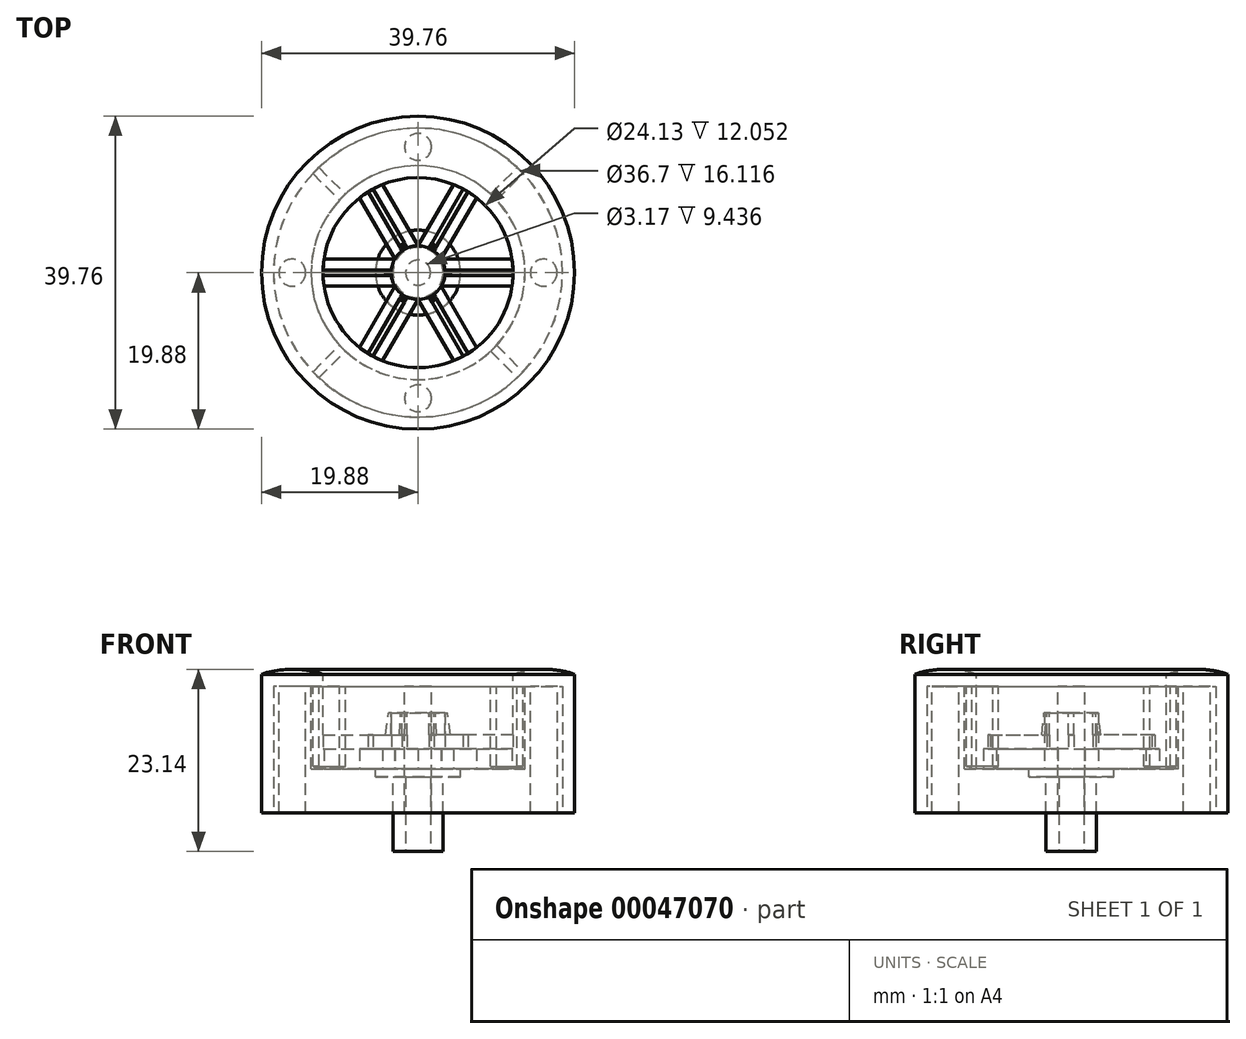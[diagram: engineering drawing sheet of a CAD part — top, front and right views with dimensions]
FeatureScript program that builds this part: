
annotation { "Feature Type Name" : "Feature", "Feature Type Description" : "" }
export const myFeature = defineFeature(function(context is Context, id is Id, definition is map)
    precondition{}
    {
        {
            var Q0;
            Q0=qCreatedBy(makeId("Top.planeOp"),FACE);
            var sketch = newSketch(context, id + "F0", { "sketchPlane" : qUnion([Q0])});
            skCircle(sketch, "E0", {"center": v(0, 0) * mm, "radius": 19.88 * mm});
            skSolve(sketch);
        }
        {
            var Q0;
            Q0=makeQuery(id+"F0.imprint","IMPRINT",FACE,{"disambiguationData":[TD([[makeQuery(id+"F0.imprint","IMPRINT",EDGE,{"derivedFrom":sQuery(id+"F0.wireOp",EDGE,"E0")}),1.0]])]});
            extrude(context, id + "F1", {"entities" : qUnion([Q0]), "endBound" : BoundingType.SYMMETRIC, "depth" : 17.64 * mm});
        }
        {
            var Q0;
            Q0=makeQuery(id+"F1.opExtrude","CAP_FACE",FACE,{"disambiguationData":[OSD([sQuery(id+"F0.wireOp",EDGE,"E0")])],"isStart":true});
            shell(context, id + "F2", {"entities" : qUnion([Q0]), "thickness" : 1.52 * mm});
        }
        {
            var Q0;
            Q0=makeQuery(id+"F1.opExtrude","CAP_FACE",FACE,{"disambiguationData":[OSD([sQuery(id+"F0.wireOp",EDGE,"E0")])],"isStart":false});
            var sketch = newSketch(context, id + "F3", { "sketchPlane" : qUnion([Q0])});
            skCircle(sketch, "E1", {"center": v(0, 0) * mm, "radius": 12.07 * mm});
            skSolve(sketch);
        }
        {
            var Q0;
            Q0 = qSketchRegion(id + "F3", true);
            extrude(context, id + "F4", {"entities" : qUnion([Q0]), "operationType" : NewBodyOperationType.REMOVE, "endBound" : BoundingType.UP_TO_NEXT, "oppositeDirection" : true, "depth" : 25.4 * mm});
        }
        {
            var Q0;
            {var subQ0=sQuery(id+"F0.wireOp",EDGE,"E0");Q0=makeQuery(id+"F2.opShell","OFFSET_FACE",FACE,{"disambiguationData":[OSD([subQ0]),TDD([makeQuery(id+"F1.opExtrude","CAP_FACE",FACE,{"disambiguationData":[OSD([subQ0])],"isStart":false})])]});}
            var sketch = newSketch(context, id + "F5", { "sketchPlane" : qUnion([Q0])});
            skCircle(sketch, "E2", {"center": v(0, 0) * mm, "radius": 13.59 * mm});
            skSolve(sketch);
        }
        {
            var Q0;
            Q0=makeQuery(id+"F5.imprint","IMPRINT",FACE,{"disambiguationData":[TD([[makeQuery(id+"F5.imprint","IMPRINT",EDGE,{"derivedFrom":sQuery(id+"F5.wireOp",EDGE,"E2")}),1.0]])]});
            extrude(context, id + "F6", {"entities" : qUnion([Q0]), "operationType" : NewBodyOperationType.ADD, "depth" : 10.53 * mm});
        }
        {
            var Q0;
            {var subQ0=sQuery(id+"F0.wireOp",EDGE,"E0");Q0=makeQuery(id+"F2.opShell","OFFSET_FACE",FACE,{"disambiguationData":[OSD([subQ0]),TDD([makeQuery(id+"F1.opExtrude","CAP_FACE",FACE,{"disambiguationData":[OSD([subQ0])],"isStart":false})])]});}
            var sketch = newSketch(context, id + "F7", { "sketchPlane" : qUnion([Q0])});
            skCircle(sketch, "E3", {"center": v(0, 15.97) * mm, "radius": 1.7 * mm});
            skLineSegment(sketch, "E4", {"start": v(0, 15.97) * mm, "end": v(0, 18.35) * mm, "construction": true});
            skLineSegment(sketch, "E5", {"start": v(0, 15.97) * mm, "end": v(0, 13.59) * mm, "construction": true});
            skCircle(sketch, "E6.MirrorC", {"center": v(0, -15.97) * mm, "radius": 1.7 * mm});
            skCircle(sketch, "E7", {"center": v(-15.97, 0) * mm, "radius": 1.71 * mm});
            skLineSegment(sketch, "E8", {"start": v(-15.97, 0) * mm, "end": v(-13.59, 0) * mm, "construction": true});
            skLineSegment(sketch, "E9", {"start": v(-15.97, 0) * mm, "end": v(-18.35, 0) * mm, "construction": true});
            skCircle(sketch, "E10.MirrorC", {"center": v(15.97, 0) * mm, "radius": 1.71 * mm});
            skSolve(sketch);
        }
        {
            var Q0;
            Q0 = qSketchRegion(id + "F7", true);
            var Q1;
            Q1=makeQuery(id+"F1.opExtrude","CAP_FACE",FACE,{"disambiguationData":[OSD([sQuery(id+"F0.wireOp",EDGE,"E0")])],"isStart":true});
            extrude(context, id + "F8", {"entities" : qUnion([Q0]), "operationType" : NewBodyOperationType.ADD, "endBound" : BoundingType.UP_TO_SURFACE, "endBoundEntityFace" : qUnion([Q1]), "depth" : 25.4 * mm});
        }
        {
            var Q0;
            Q0=makeQuery(id+"F6.opExtrude","CAP_FACE",FACE,{"disambiguationData":[OSD([sQuery(id+"F0.wireOp",EDGE,"E0"),sQuery(id+"F3.wireOp",EDGE,"E1"),sQuery(id+"F5.wireOp",EDGE,"E2")])],"isStart":false});
            cPlane(context, id + "F9", {"entities" : qUnion([Q0]), "cplaneType" : CPlaneType.OFFSET, "offset" : 0 * mm, "width" : 152.4 * mm, "height" : 152.4 * mm});
        }
        {
            var Q0;
            Q0=qCreatedBy(id+"F9.planeOp",FACE);
            var sketch = newSketch(context, id + "F10", { "sketchPlane" : qUnion([Q0])});
            skCircle(sketch, "E11", {"center": v(0, 0) * mm, "radius": 5.4 * mm});
            skSolve(sketch);
        }
        {
            var Q0;
            Q0=makeQuery(id+"F10.imprint","IMPRINT",FACE,{"disambiguationData":[TD([[makeQuery(id+"F10.imprint","IMPRINT",EDGE,{"derivedFrom":sQuery(id+"F10.wireOp",EDGE,"E11")}),1.0]])]});
            extrude(context, id + "F11", {"entities" : qUnion([Q0]), "depth" : 1.02 * mm});
        }
        {
            var Q0;
            Q0=makeQuery(id+"F11.opExtrude","CAP_FACE",FACE,{"disambiguationData":[OSD([sQuery(id+"F10.wireOp",EDGE,"E11")])],"isStart":true});
            var sketch = newSketch(context, id + "F12", { "sketchPlane" : qUnion([Q0])});
            skCircle(sketch, "E12", {"center": v(0, 0) * mm, "radius": 3.42 * mm});
            skSolve(sketch);
        }
        {
            var Q0;
            Q0=makeQuery(id+"F12.imprint","IMPRINT",FACE,{"disambiguationData":[TD([[makeQuery(id+"F12.imprint","IMPRINT",EDGE,{"derivedFrom":sQuery(id+"F12.wireOp",EDGE,"E12")}),1.0]])]});
            extrude(context, id + "F13", {"entities" : qUnion([Q0]), "operationType" : NewBodyOperationType.ADD, "depth" : 7.11 * mm});
        }
        {
            var Q0;
            Q0=makeQuery(id+"F11.opExtrude","CAP_FACE",FACE,{"disambiguationData":[OSD([sQuery(id+"F10.wireOp",EDGE,"E11")])],"isStart":true});
            var sketch = newSketch(context, id + "F14", { "sketchPlane" : qUnion([Q0])});
            skLineSegment(sketch, "E13", {"start": v(-12.07, 0) * mm, "end": v(-3.42, 0) * mm, "construction": true});
            skLineSegment(sketch, "E14.1.0", {"start": v(6.03, -10.45) * mm, "end": v(1.7, -2.96) * mm, "construction": true});
            skLineSegment(sketch, "E14.2.0", {"start": v(6.03, 10.45) * mm, "end": v(1.7, 2.96) * mm, "construction": true});
            skPoint(sketch, "E14.center", {"position": v(0, 0) * mm});
            skLineSegment(sketch, "E15", {"start": v(4.5, 11.2) * mm, "end": v(0, 3.4) * mm});
            skLineSegment(sketch, "E16", {"start": v(7.44, 9.5) * mm, "end": v(2.94, 1.7) * mm});
            skLineSegment(sketch, "E17.1.0", {"start": v(-11.95, -1.7) * mm, "end": v(-2.94, -1.7) * mm});
            skLineSegment(sketch, "E17.1.1", {"start": v(-11.95, 1.7) * mm, "end": v(-2.94, 1.7) * mm});
            skLineSegment(sketch, "E17.2.0", {"start": v(7.44, -9.5) * mm, "end": v(2.94, -1.7) * mm});
            skLineSegment(sketch, "E17.2.1", {"start": v(4.5, -11.2) * mm, "end": v(0, -3.4) * mm});
            skCircle(sketch, "E18.0", {"center": v(0, 0) * mm, "radius": 3.42 * mm});
            skLineSegment(sketch, "E19.trimOffspring", {"start": v(0, -3.4) * mm, "end": v(-4.5, -11.2) * mm});
            skLineSegment(sketch, "E20.trimOffspring", {"start": v(-1.7, -2.96) * mm, "end": v(-6.03, -10.45) * mm, "construction": true});
            skLineSegment(sketch, "E21.trimOffspring", {"start": v(2.94, -1.7) * mm, "end": v(11.95, -1.7) * mm});
            skLineSegment(sketch, "E22.trimOffspring", {"start": v(-2.94, -1.7) * mm, "end": v(-7.44, -9.5) * mm});
            skLineSegment(sketch, "E23.trimOffspring", {"start": v(-2.94, 1.7) * mm, "end": v(-7.44, 9.5) * mm});
            skLineSegment(sketch, "E24.trimOffspring", {"start": v(2.94, 1.7) * mm, "end": v(11.95, 1.7) * mm});
            skLineSegment(sketch, "E25.trimOffspring", {"start": v(0, 3.4) * mm, "end": v(-4.5, 11.2) * mm});
            skLineSegment(sketch, "E26.trimOffspring", {"start": v(3.42, 0) * mm, "end": v(12.07, 0) * mm, "construction": true});
            skLineSegment(sketch, "E27.trimOffspring", {"start": v(-1.7, 2.96) * mm, "end": v(-6.03, 10.45) * mm, "construction": true});
            skArc(sketch, "E28.0", {"start": v(-11.95, 1.7) * mm, "mid": v(-12.07, 0) * mm, "end": v(-11.95, -1.7) * mm});
            skArc(sketch, "E29.trimOffspring", {"start": v(-4.5, 11.2) * mm, "mid": v(-6.03, 10.45) * mm, "end": v(-7.44, 9.5) * mm});
            skArc(sketch, "E30.trimOffspring", {"start": v(7.44, 9.5) * mm, "mid": v(6.03, 10.45) * mm, "end": v(4.5, 11.2) * mm});
            skArc(sketch, "E31.trimOffspring", {"start": v(11.95, -1.7) * mm, "mid": v(12.07, 0) * mm, "end": v(11.95, 1.7) * mm});
            skArc(sketch, "E32.trimOffspring", {"start": v(4.5, -11.2) * mm, "mid": v(6.03, -10.45) * mm, "end": v(7.44, -9.5) * mm});
            skArc(sketch, "E33.trimOffspring", {"start": v(-7.44, -9.5) * mm, "mid": v(-6.03, -10.45) * mm, "end": v(-4.5, -11.2) * mm});
            skSolve(sketch);
        }
        {
            var Q0;
            {var subQ0=sQuery(id+"F14.wireOp",EDGE,"E28.0");Q0=makeQuery(id+"F14.imprint","IMPRINT",FACE,{"disambiguationData":[TD([[makeQuery(id+"F14.imprint","IMPRINT",EDGE,{"derivedFrom":subQ0}),1.0]])]});}
            var Q1;
            {var subQ0=sQuery(id+"F14.wireOp",EDGE,"E18.0");var subQ1=sQuery(id+"F14.wireOp",EDGE,"E17.1.0");var subQ2=makeQuery(id+"F14.imprint","INTERSECT",VERTEX,{"derivedFrom":[subQ1,subQ0]});Q1=makeQuery(id+"F14.imprint","IMPRINT",FACE,{"disambiguationData":[TD([[makeQuery(id+"F14.imprint","IMPRINT",EDGE,{"disambiguationData":[TD([[subQ2,1.0]])],"derivedFrom":subQ1}),1.0]])]});}
            var Q2;
            {var subQ0=sQuery(id+"F14.wireOp",EDGE,"E25.trimOffspring");var subQ1=sQuery(id+"F14.wireOp",EDGE,"E18.0");var subQ2=makeQuery(id+"F14.imprint","INTERSECT",VERTEX,{"derivedFrom":[subQ1,subQ0]});Q2=makeQuery(id+"F14.imprint","IMPRINT",FACE,{"disambiguationData":[TD([[makeQuery(id+"F14.imprint","IMPRINT",EDGE,{"disambiguationData":[TD([[subQ2,-1.0]])],"derivedFrom":subQ1}),-1.0]])]});}
            var Q3;
            {var subQ0=sQuery(id+"F14.wireOp",EDGE,"E29.trimOffspring");Q3=makeQuery(id+"F14.imprint","IMPRINT",FACE,{"disambiguationData":[TD([[makeQuery(id+"F14.imprint","IMPRINT",EDGE,{"derivedFrom":subQ0}),1.0]])]});}
            var Q4;
            {var subQ0=sQuery(id+"F14.wireOp",EDGE,"E30.trimOffspring");Q4=makeQuery(id+"F14.imprint","IMPRINT",FACE,{"disambiguationData":[TD([[makeQuery(id+"F14.imprint","IMPRINT",EDGE,{"derivedFrom":subQ0}),1.0]])]});}
            var Q5;
            {var subQ0=sQuery(id+"F14.wireOp",EDGE,"E18.0");var subQ1=sQuery(id+"F14.wireOp",EDGE,"E15");var subQ2=makeQuery(id+"F14.imprint","INTERSECT",VERTEX,{"derivedFrom":[subQ1,subQ0]});Q5=makeQuery(id+"F14.imprint","IMPRINT",FACE,{"disambiguationData":[TD([[makeQuery(id+"F14.imprint","IMPRINT",EDGE,{"disambiguationData":[TD([[subQ2,1.0]])],"derivedFrom":subQ1}),1.0]])]});}
            var Q6;
            {var subQ0=sQuery(id+"F14.wireOp",EDGE,"E24.trimOffspring");var subQ1=sQuery(id+"F14.wireOp",EDGE,"E18.0");var subQ2=makeQuery(id+"F14.imprint","INTERSECT",VERTEX,{"derivedFrom":[subQ1,subQ0]});Q6=makeQuery(id+"F14.imprint","IMPRINT",FACE,{"disambiguationData":[TD([[makeQuery(id+"F14.imprint","IMPRINT",EDGE,{"disambiguationData":[TD([[subQ2,1.0]])],"derivedFrom":subQ1}),-1.0]])]});}
            var Q7;
            {var subQ0=sQuery(id+"F14.wireOp",EDGE,"E31.trimOffspring");Q7=makeQuery(id+"F14.imprint","IMPRINT",FACE,{"disambiguationData":[TD([[makeQuery(id+"F14.imprint","IMPRINT",EDGE,{"derivedFrom":subQ0}),1.0]])]});}
            var Q8;
            {var subQ0=sQuery(id+"F14.wireOp",EDGE,"E18.0");var subQ1=sQuery(id+"F14.wireOp",EDGE,"E17.2.0");var subQ2=makeQuery(id+"F14.imprint","INTERSECT",VERTEX,{"derivedFrom":[subQ1,subQ0]});Q8=makeQuery(id+"F14.imprint","IMPRINT",FACE,{"disambiguationData":[TD([[makeQuery(id+"F14.imprint","IMPRINT",EDGE,{"disambiguationData":[TD([[subQ2,1.0]])],"derivedFrom":subQ1}),1.0]])]});}
            var Q9;
            {var subQ0=sQuery(id+"F14.wireOp",EDGE,"E32.trimOffspring");Q9=makeQuery(id+"F14.imprint","IMPRINT",FACE,{"disambiguationData":[TD([[makeQuery(id+"F14.imprint","IMPRINT",EDGE,{"derivedFrom":subQ0}),1.0]])]});}
            var Q10;
            {var subQ0=sQuery(id+"F14.wireOp",EDGE,"E22.trimOffspring");var subQ1=sQuery(id+"F14.wireOp",EDGE,"E18.0");var subQ2=makeQuery(id+"F14.imprint","INTERSECT",VERTEX,{"derivedFrom":[subQ1,subQ0]});Q10=makeQuery(id+"F14.imprint","IMPRINT",FACE,{"disambiguationData":[TD([[makeQuery(id+"F14.imprint","IMPRINT",EDGE,{"disambiguationData":[TD([[subQ2,-1.0]])],"derivedFrom":subQ1}),-1.0]])]});}
            var Q11;
            {var subQ0=sQuery(id+"F14.wireOp",EDGE,"E33.trimOffspring");Q11=makeQuery(id+"F14.imprint","IMPRINT",FACE,{"disambiguationData":[TD([[makeQuery(id+"F14.imprint","IMPRINT",EDGE,{"derivedFrom":subQ0}),1.0]])]});}
            extrude(context, id + "F15", {"entities" : qUnion([Q0, Q1, Q2, Q3, Q4, Q5, Q6, Q7, Q8, Q9, Q10, Q11]), "depth" : 2.54 * mm});
        }
        {
            var Q0;
            Q0=makeQuery(id+"F1.opExtrude","SWEPT_BODY",BODY,{"disambiguationData":[OSD([sQuery(id+"F0.wireOp",EDGE,"E0")])]});
            var Q1;
            Q1=makeQuery(id+"F11.opExtrude","SWEPT_BODY",BODY,{"disambiguationData":[OSD([sQuery(id+"F10.wireOp",EDGE,"E11")])]});
            var Q2;
            Q2=makeQuery(id+"F15.opExtrude","SWEPT_BODY",BODY,{"disambiguationData":[OSD([sQuery(id+"F14.wireOp",EDGE,"E15"),sQuery(id+"F14.wireOp",EDGE,"E16"),sQuery(id+"F14.wireOp",EDGE,"E18.0"),sQuery(id+"F14.wireOp",EDGE,"E30.trimOffspring")])]});
            var Q3;
            Q3=makeQuery(id+"F15.opExtrude","SWEPT_BODY",BODY,{"disambiguationData":[OSD([sQuery(id+"F14.wireOp",EDGE,"E17.1.0"),sQuery(id+"F14.wireOp",EDGE,"E17.1.1"),sQuery(id+"F14.wireOp",EDGE,"E18.0"),sQuery(id+"F14.wireOp",EDGE,"E28.0")])]});
            var Q4;
            Q4=makeQuery(id+"F15.opExtrude","SWEPT_BODY",BODY,{"disambiguationData":[OSD([sQuery(id+"F14.wireOp",EDGE,"E17.2.0"),sQuery(id+"F14.wireOp",EDGE,"E17.2.1"),sQuery(id+"F14.wireOp",EDGE,"E18.0"),sQuery(id+"F14.wireOp",EDGE,"E32.trimOffspring")])]});
            var Q5;
            Q5=makeQuery(id+"F15.opExtrude","SWEPT_BODY",BODY,{"disambiguationData":[OSD([sQuery(id+"F14.wireOp",EDGE,"E18.0"),sQuery(id+"F14.wireOp",EDGE,"E23.trimOffspring"),sQuery(id+"F14.wireOp",EDGE,"E25.trimOffspring"),sQuery(id+"F14.wireOp",EDGE,"E29.trimOffspring")])]});
            var Q6;
            Q6=makeQuery(id+"F15.opExtrude","SWEPT_BODY",BODY,{"disambiguationData":[OSD([sQuery(id+"F14.wireOp",EDGE,"E18.0"),sQuery(id+"F14.wireOp",EDGE,"E19.trimOffspring"),sQuery(id+"F14.wireOp",EDGE,"E22.trimOffspring"),sQuery(id+"F14.wireOp",EDGE,"E33.trimOffspring")])]});
            var Q7;
            Q7=makeQuery(id+"F15.opExtrude","SWEPT_BODY",BODY,{"disambiguationData":[OSD([sQuery(id+"F14.wireOp",EDGE,"E18.0"),sQuery(id+"F14.wireOp",EDGE,"E21.trimOffspring"),sQuery(id+"F14.wireOp",EDGE,"E24.trimOffspring"),sQuery(id+"F14.wireOp",EDGE,"E31.trimOffspring")])]});
            booleanBodies(context, id + "F16", {"operationType" : BooleanOperationType.UNION, "tools" : qUnion([Q0, Q1, Q2, Q3, Q4, Q5, Q6, Q7])});
        }
        {
            var Q0;
            {var subQ0=sQuery(id+"F0.wireOp",EDGE,"E0");Q0=makeQuery(id+"F2.opShell","OFFSET_FACE",FACE,{"disambiguationData":[OSD([subQ0]),TDD([makeQuery(id+"F1.opExtrude","CAP_FACE",FACE,{"disambiguationData":[OSD([subQ0])],"isStart":false})])]});}
            var sketch = newSketch(context, id + "F17", { "sketchPlane" : qUnion([Q0])});
            skArc(sketch, "E34.0", {"start": v(12.6, -13.35) * mm, "mid": v(12.98, -12.98) * mm, "end": v(13.35, -12.6) * mm});
            skArc(sketch, "E35.0", {"start": v(9.22, -9.98) * mm, "mid": v(9.6, -9.6) * mm, "end": v(9.98, -9.22) * mm});
            skLineSegment(sketch, "E36", {"start": v(-14.05, -14.05) * mm, "end": v(14.05, 14.05) * mm, "construction": true});
            skLineSegment(sketch, "E37", {"start": v(-13.35, -12.6) * mm, "end": v(-9.98, -9.22) * mm});
            skLineSegment(sketch, "E38", {"start": v(-12.6, -13.35) * mm, "end": v(-9.22, -9.98) * mm});
            skLineSegment(sketch, "E39", {"start": v(-12.98, 12.98) * mm, "end": v(12.98, -12.98) * mm, "construction": true});
            skLineSegment(sketch, "E40", {"start": v(9.22, -9.98) * mm, "end": v(12.6, -13.35) * mm});
            skLineSegment(sketch, "E41", {"start": v(9.98, -9.22) * mm, "end": v(13.35, -12.6) * mm});
            skArc(sketch, "E42.trimOffspring", {"start": v(-13.35, -12.6) * mm, "mid": v(-12.98, -12.98) * mm, "end": v(-12.6, -13.35) * mm});
            skArc(sketch, "E43.trimOffspring", {"start": v(-9.98, -9.22) * mm, "mid": v(-9.6, -9.6) * mm, "end": v(-9.22, -9.98) * mm});
            skArc(sketch, "E44.MirrorCS", {"start": v(9.22, 9.98) * mm, "mid": v(9.6, 9.6) * mm, "end": v(9.98, 9.22) * mm});
            skArc(sketch, "E45.MirrorCS", {"start": v(-13.35, 12.6) * mm, "mid": v(-12.98, 12.98) * mm, "end": v(-12.6, 13.35) * mm});
            skArc(sketch, "E46.MirrorCS", {"start": v(12.6, 13.35) * mm, "mid": v(12.98, 12.98) * mm, "end": v(13.35, 12.6) * mm});
            skArc(sketch, "E47.MirrorCS", {"start": v(-9.98, 9.22) * mm, "mid": v(-9.6, 9.6) * mm, "end": v(-9.22, 9.98) * mm});
            skLineSegment(sketch, "E48.MirrorCS", {"start": v(-14.05, 14.05) * mm, "end": v(14.05, -14.05) * mm, "construction": true});
            skLineSegment(sketch, "E49.MirrorCS", {"start": v(-13.35, 12.6) * mm, "end": v(-9.98, 9.22) * mm});
            skLineSegment(sketch, "E50.MirrorCS", {"start": v(-12.6, 13.35) * mm, "end": v(-9.22, 9.98) * mm});
            skLineSegment(sketch, "E51.MirrorCS", {"start": v(-12.98, -12.98) * mm, "end": v(12.98, 12.98) * mm, "construction": true});
            skLineSegment(sketch, "E52.MirrorCS", {"start": v(9.98, 9.22) * mm, "end": v(13.35, 12.6) * mm});
            skLineSegment(sketch, "E53.MirrorCS", {"start": v(9.22, 9.98) * mm, "end": v(12.6, 13.35) * mm});
            skSolve(sketch);
        }
        {
            var Q0;
            Q0 = qSketchRegion(id + "F17", true);
            var Q1;
            {var subQ0=sQuery(id+"F14.wireOp",EDGE,"E18.0");Q1=makeQuery(id+"F16.opBoolean","MERGE",FACE,{"derivedFrom":[makeQuery(id+"F6.opExtrude","CAP_FACE",FACE,{"disambiguationData":[OSD([sQuery(id+"F0.wireOp",EDGE,"E0"),sQuery(id+"F3.wireOp",EDGE,"E1"),sQuery(id+"F5.wireOp",EDGE,"E2")])],"isStart":false}),makeQuery(id+"F15.opExtrude","CAP_FACE",FACE,{"disambiguationData":[OSD([sQuery(id+"F14.wireOp",EDGE,"E15"),sQuery(id+"F14.wireOp",EDGE,"E16"),subQ0,sQuery(id+"F14.wireOp",EDGE,"E30.trimOffspring")])],"isStart":true}),makeQuery(id+"F15.opExtrude","CAP_FACE",FACE,{"disambiguationData":[OSD([sQuery(id+"F14.wireOp",EDGE,"E17.1.0"),sQuery(id+"F14.wireOp",EDGE,"E17.1.1"),subQ0,sQuery(id+"F14.wireOp",EDGE,"E28.0")])],"isStart":true}),makeQuery(id+"F15.opExtrude","CAP_FACE",FACE,{"disambiguationData":[OSD([sQuery(id+"F14.wireOp",EDGE,"E17.2.0"),sQuery(id+"F14.wireOp",EDGE,"E17.2.1"),subQ0,sQuery(id+"F14.wireOp",EDGE,"E32.trimOffspring")])],"isStart":true}),makeQuery(id+"F15.opExtrude","CAP_FACE",FACE,{"disambiguationData":[OSD([subQ0,sQuery(id+"F14.wireOp",EDGE,"E23.trimOffspring"),sQuery(id+"F14.wireOp",EDGE,"E25.trimOffspring"),sQuery(id+"F14.wireOp",EDGE,"E29.trimOffspring")])],"isStart":true}),makeQuery(id+"F15.opExtrude","CAP_FACE",FACE,{"disambiguationData":[OSD([subQ0,sQuery(id+"F14.wireOp",EDGE,"E19.trimOffspring"),sQuery(id+"F14.wireOp",EDGE,"E22.trimOffspring"),sQuery(id+"F14.wireOp",EDGE,"E33.trimOffspring")])],"isStart":true}),makeQuery(id+"F15.opExtrude","CAP_FACE",FACE,{"disambiguationData":[OSD([subQ0,sQuery(id+"F14.wireOp",EDGE,"E21.trimOffspring"),sQuery(id+"F14.wireOp",EDGE,"E24.trimOffspring"),sQuery(id+"F14.wireOp",EDGE,"E31.trimOffspring")])],"isStart":true})]});}
            extrude(context, id + "F18", {"entities" : qUnion([Q0]), "operationType" : NewBodyOperationType.ADD, "endBoundEntityFace" : qUnion([Q1]), "depth" : 10.16 * mm});
        }
        {
            var Q0;
            Q0=qCreatedBy(makeId("Front.planeOp"),FACE);
            var sketch = newSketch(context, id + "F19", { "sketchPlane" : qUnion([Q0])});
            skLineSegment(sketch, "E54", {"start": v(12.07, 8.82) * mm, "end": v(12.07, -0.7) * mm, "construction": true});
            skLineSegment(sketch, "E55", {"start": v(-12.07, -0.7) * mm, "end": v(-12.07, 8.82) * mm, "construction": true});
            skLineSegment(sketch, "E56", {"start": v(19.88, 8.82) * mm, "end": v(19.88, -8.82) * mm, "construction": true});
            skArc(sketch, "E57", {"start": v(19.88, 8.82) * mm, "mid": v(15.97, 9.46) * mm, "end": v(12.07, 8.82) * mm});
            skLineSegment(sketch, "E58", {"start": v(12.07, 8.82) * mm, "end": v(19.88, 8.82) * mm});
            skSolve(sketch);
        }
        {
            var Q0;
            Q0=makeQuery(id+"F19.imprint","IMPRINT",FACE,{"disambiguationData":[TD([[makeQuery(id+"F19.imprint","IMPRINT",EDGE,{"derivedFrom":sQuery(id+"F19.wireOp",EDGE,"E57")}),1.0]])]});
            var Q1;
            Q1=makeQuery(id+"F13.opExtrude","CAP_EDGE",EDGE,{"disambiguationData":[OSD([sQuery(id+"F12.wireOp",EDGE,"E12")])],"isStart":false});
            revolve(context, id + "F20", {"operationType" : NewBodyOperationType.ADD, "entities" : qUnion([Q0]), "axis" : qUnion([Q1]), "revolveType" : RevolveType.FULL});
        }
        {
            var Q0;
            Q0=makeQuery(id+"F15.opExtrude","CAP_FACE",FACE,{"disambiguationData":[OSD([sQuery(id+"F14.wireOp",EDGE,"E17.2.0"),sQuery(id+"F14.wireOp",EDGE,"E17.2.1"),sQuery(id+"F14.wireOp",EDGE,"E18.0"),sQuery(id+"F14.wireOp",EDGE,"E32.trimOffspring")])],"isStart":false});
            var sketch = newSketch(context, id + "F21", { "sketchPlane" : qUnion([Q0])});
            skLineSegment(sketch, "E59.0", {"start": v(-0.01, 3.42) * mm, "end": v(-4.5, 11.2) * mm, "construction": true});
            skLineSegment(sketch, "E60.0", {"start": v(-2.95, 1.72) * mm, "end": v(-7.44, 9.5) * mm, "construction": true});
            skLineSegment(sketch, "E61", {"start": v(-6.03, 10.45) * mm, "end": v(6.03, -10.45) * mm, "construction": true});
            skLineSegment(sketch, "E62", {"start": v(-6.34, 10.27) * mm, "end": v(-2, 2.76) * mm});
            skLineSegment(sketch, "E63", {"start": v(-5.72, 10.62) * mm, "end": v(-1.4, 3.12) * mm});
            skArc(sketch, "E64.0", {"start": v(12.06, -0.36) * mm, "mid": v(12.06, 0) * mm, "end": v(12.06, 0.36) * mm});
            skArc(sketch, "E65.0", {"start": v(2, 2.76) * mm, "mid": v(1.7, 2.96) * mm, "end": v(1.4, 3.12) * mm});
            skLineSegment(sketch, "E66.1.0", {"start": v(-12.07, 0) * mm, "end": v(12.07, 0) * mm, "construction": true});
            skLineSegment(sketch, "E66.1.1", {"start": v(-12.06, 0.36) * mm, "end": v(-3.4, 0.36) * mm});
            skLineSegment(sketch, "E66.1.2", {"start": v(-12.06, -0.36) * mm, "end": v(-3.4, -0.36) * mm});
            skLineSegment(sketch, "E66.2.0", {"start": v(-6.03, -10.45) * mm, "end": v(6.03, 10.45) * mm, "construction": true});
            skLineSegment(sketch, "E66.2.1", {"start": v(-6.34, -10.27) * mm, "end": v(-2, -2.76) * mm});
            skLineSegment(sketch, "E66.2.2", {"start": v(-5.72, -10.62) * mm, "end": v(-1.4, -3.12) * mm});
            skLineSegment(sketch, "E66.3.0", {"start": v(6.03, -10.45) * mm, "end": v(-6.03, 10.45) * mm, "construction": true});
            skLineSegment(sketch, "E66.3.1", {"start": v(5.72, -10.62) * mm, "end": v(1.4, -3.12) * mm});
            skLineSegment(sketch, "E66.3.2", {"start": v(6.34, -10.27) * mm, "end": v(2, -2.76) * mm});
            skLineSegment(sketch, "E66.4.0", {"start": v(12.07, 0) * mm, "end": v(-12.07, 0) * mm, "construction": true});
            skLineSegment(sketch, "E66.4.1", {"start": v(12.06, -0.36) * mm, "end": v(3.4, -0.36) * mm});
            skLineSegment(sketch, "E66.4.2", {"start": v(12.06, 0.36) * mm, "end": v(3.4, 0.36) * mm});
            skLineSegment(sketch, "E66.5.0", {"start": v(6.03, 10.45) * mm, "end": v(-6.03, -10.45) * mm, "construction": true});
            skLineSegment(sketch, "E66.5.1", {"start": v(6.34, 10.27) * mm, "end": v(2, 2.76) * mm});
            skLineSegment(sketch, "E66.5.2", {"start": v(5.72, 10.62) * mm, "end": v(1.4, 3.12) * mm});
            skArc(sketch, "E67.trimOffspring", {"start": v(-1.4, 3.12) * mm, "mid": v(-1.7, 2.96) * mm, "end": v(-2, 2.76) * mm});
            skArc(sketch, "E68.trimOffspring", {"start": v(-3.4, 0.36) * mm, "mid": v(-3.42, 0) * mm, "end": v(-3.4, -0.36) * mm});
            skArc(sketch, "E69.trimOffspring", {"start": v(-2, -2.76) * mm, "mid": v(-1.7, -2.96) * mm, "end": v(-1.4, -3.12) * mm});
            skArc(sketch, "E70.trimOffspring", {"start": v(1.4, -3.12) * mm, "mid": v(1.7, -2.96) * mm, "end": v(2, -2.76) * mm});
            skArc(sketch, "E71.trimOffspring", {"start": v(3.4, -0.36) * mm, "mid": v(3.42, 0) * mm, "end": v(3.4, 0.36) * mm});
            skArc(sketch, "E72.trimOffspring", {"start": v(5.72, -10.62) * mm, "mid": v(6.03, -10.45) * mm, "end": v(6.34, -10.27) * mm});
            skArc(sketch, "E73.trimOffspring", {"start": v(-6.34, -10.27) * mm, "mid": v(-6.03, -10.45) * mm, "end": v(-5.72, -10.62) * mm});
            skArc(sketch, "E74.trimOffspring", {"start": v(-12.06, 0.36) * mm, "mid": v(-12.07, 0) * mm, "end": v(-12.06, -0.36) * mm});
            skArc(sketch, "E75.trimOffspring", {"start": v(-5.72, 10.62) * mm, "mid": v(-6.03, 10.45) * mm, "end": v(-6.34, 10.27) * mm});
            skArc(sketch, "E76.trimOffspring", {"start": v(6.34, 10.27) * mm, "mid": v(6.03, 10.45) * mm, "end": v(5.72, 10.62) * mm});
            skSolve(sketch);
        }
        {
            var Q0;
            Q0 = qSketchRegion(id + "F21", true);
            extrude(context, id + "F22", {"entities" : qUnion([Q0]), "operationType" : NewBodyOperationType.ADD, "depth" : 1.78 * mm});
        }
        {
            var Q0;
            Q0=makeQuery(id+"F11.opExtrude","CAP_FACE",FACE,{"disambiguationData":[OSD([sQuery(id+"F10.wireOp",EDGE,"E11")])],"isStart":false});
            var sketch = newSketch(context, id + "F23", { "sketchPlane" : qUnion([Q0])});
            skCircle(sketch, "E77", {"center": v(0, 0) * mm, "radius": 3.2 * mm});
            skSolve(sketch);
        }
        {
            var Q0;
            Q0=makeQuery(id+"F23.imprint","IMPRINT",FACE,{"disambiguationData":[TD([[makeQuery(id+"F23.imprint","IMPRINT",EDGE,{"derivedFrom":sQuery(id+"F23.wireOp",EDGE,"E77")}),1.0]])]});
            extrude(context, id + "F24", {"entities" : qUnion([Q0]), "operationType" : NewBodyOperationType.ADD, "depth" : 9.44 * mm});
        }
        {
            var Q0;
            Q0=makeQuery(id+"F24.opExtrude","CAP_FACE",FACE,{"disambiguationData":[OSD([sQuery(id+"F23.wireOp",EDGE,"E77")])],"isStart":false});
            var sketch = newSketch(context, id + "F25", { "sketchPlane" : qUnion([Q0])});
            skCircle(sketch, "E78", {"center": v(0, 0) * mm, "radius": 1.59 * mm});
            skSolve(sketch);
        }
        {
            var Q0;
            Q0=makeQuery(id+"F25.imprint","IMPRINT",FACE,{"disambiguationData":[TD([[makeQuery(id+"F25.imprint","IMPRINT",EDGE,{"derivedFrom":sQuery(id+"F25.wireOp",EDGE,"E78")}),1.0]])]});
            var Q1;
            Q1=makeQuery(id+"F11.opExtrude","CAP_FACE",FACE,{"disambiguationData":[OSD([sQuery(id+"F10.wireOp",EDGE,"E11")])],"isStart":false});
            extrude(context, id + "F26", {"entities" : qUnion([Q0]), "operationType" : NewBodyOperationType.REMOVE, "endBound" : BoundingType.UP_TO_SURFACE, "oppositeDirection" : true, "endBoundEntityFace" : qUnion([Q1]), "depth" : 25.4 * mm});
        }
        {
            var Q0;
            Q0=makeQuery(id+"F22.opExtrude","CAP_FACE",FACE,{"disambiguationData":[OSD([sQuery(id+"F21.wireOp",EDGE,"E64.0"),sQuery(id+"F21.wireOp",EDGE,"E66.4.1"),sQuery(id+"F21.wireOp",EDGE,"E66.4.2"),sQuery(id+"F21.wireOp",EDGE,"E71.trimOffspring")])],"isStart":false});
            var sketch = newSketch(context, id + "F27", { "sketchPlane" : qUnion([Q0])});
            skLineSegment(sketch, "E79", {"start": v(3.4, 0.36) * mm, "end": v(4.1, 0.36) * mm, "construction": true});
            skLineSegment(sketch, "E80", {"start": v(3.4, -0.36) * mm, "end": v(4.1, -0.36) * mm, "construction": true});
            skArc(sketch, "E81.0", {"start": v(3.4, -0.36) * mm, "mid": v(3.42, 0) * mm, "end": v(3.4, 0.36) * mm});
            skLineSegment(sketch, "E82", {"start": v(4.1, 0.36) * mm, "end": v(4.1, -0.36) * mm});
            skSolve(sketch);
        }
        {
            var Q0;
            Q0=makeQuery(id+"F13.opExtrude","CAP_FACE",FACE,{"disambiguationData":[OSD([sQuery(id+"F12.wireOp",EDGE,"E12")])],"isStart":false});
            var sketch = newSketch(context, id + "F28", { "sketchPlane" : qUnion([Q0])});
            skArc(sketch, "E83.0", {"start": v(3.4, -0.36) * mm, "mid": v(3.42, 0) * mm, "end": v(3.4, 0.36) * mm});
            skLineSegment(sketch, "E84", {"start": v(3.4, 0.36) * mm, "end": v(3.77, 0.36) * mm});
            skLineSegment(sketch, "E85", {"start": v(3.4, -0.36) * mm, "end": v(3.77, -0.36) * mm});
            skLineSegment(sketch, "E86", {"start": v(3.77, 0.36) * mm, "end": v(3.77, -0.36) * mm});
            skSolve(sketch);
        }
        {
            var Q1;
            {var subQ0=sQuery(id+"F27.wireOp",EDGE,"E81.0");Q1=makeQuery(id+"F27.imprint","IMPRINT",FACE,{"disambiguationData":[TD([[makeQuery(id+"F27.imprint","IMPRINT",EDGE,{"derivedFrom":subQ0}),-1.0]])]});}
            var Q2;
            Q2=makeQuery(id+"F28.imprint","IMPRINT",FACE,{"disambiguationData":[TD([[makeQuery(id+"F28.imprint","IMPRINT",EDGE,{"derivedFrom":sQuery(id+"F28.wireOp",EDGE,"E83.0")}),-1.0]])]});
            loft(context, id + "F29", {"sheetProfilesArray" : [{ "sheetProfileEntities" : qUnion([Q1]) }, { "sheetProfileEntities" : qUnion([Q2]) }]});
        }
        {
            var Q0;
            {var subQ0=sQuery(id+"F27.wireOp",EDGE,"E81.0");Q0=makeQuery(id+"F29.opLoft","SWEPT_BODY",BODY,{"disambiguationData":[OSD([makeQuery(id+"F27.imprint","IMPRINT",FACE,{"disambiguationData":[TD([[makeQuery(id+"F27.imprint","IMPRINT",EDGE,{"derivedFrom":subQ0}),-1.0]])]}),makeQuery(id+"F28.imprint","IMPRINT",FACE,{"disambiguationData":[TD([[makeQuery(id+"F28.imprint","IMPRINT",EDGE,{"derivedFrom":sQuery(id+"F28.wireOp",EDGE,"E83.0")}),-1.0]])]})])]});}
            var Q1;
            Q1=makeQuery(id+"F13.opExtrude","CAP_EDGE",EDGE,{"disambiguationData":[OSD([sQuery(id+"F12.wireOp",EDGE,"E12")])],"isStart":false});
            circularPattern(context, id + "F30", {"entities" : qUnion([Q0]), "axis" : qUnion([Q1]), "angle" : 360 * degree, "instanceCount" : 6, "equalSpace" : true});
        }
    });
